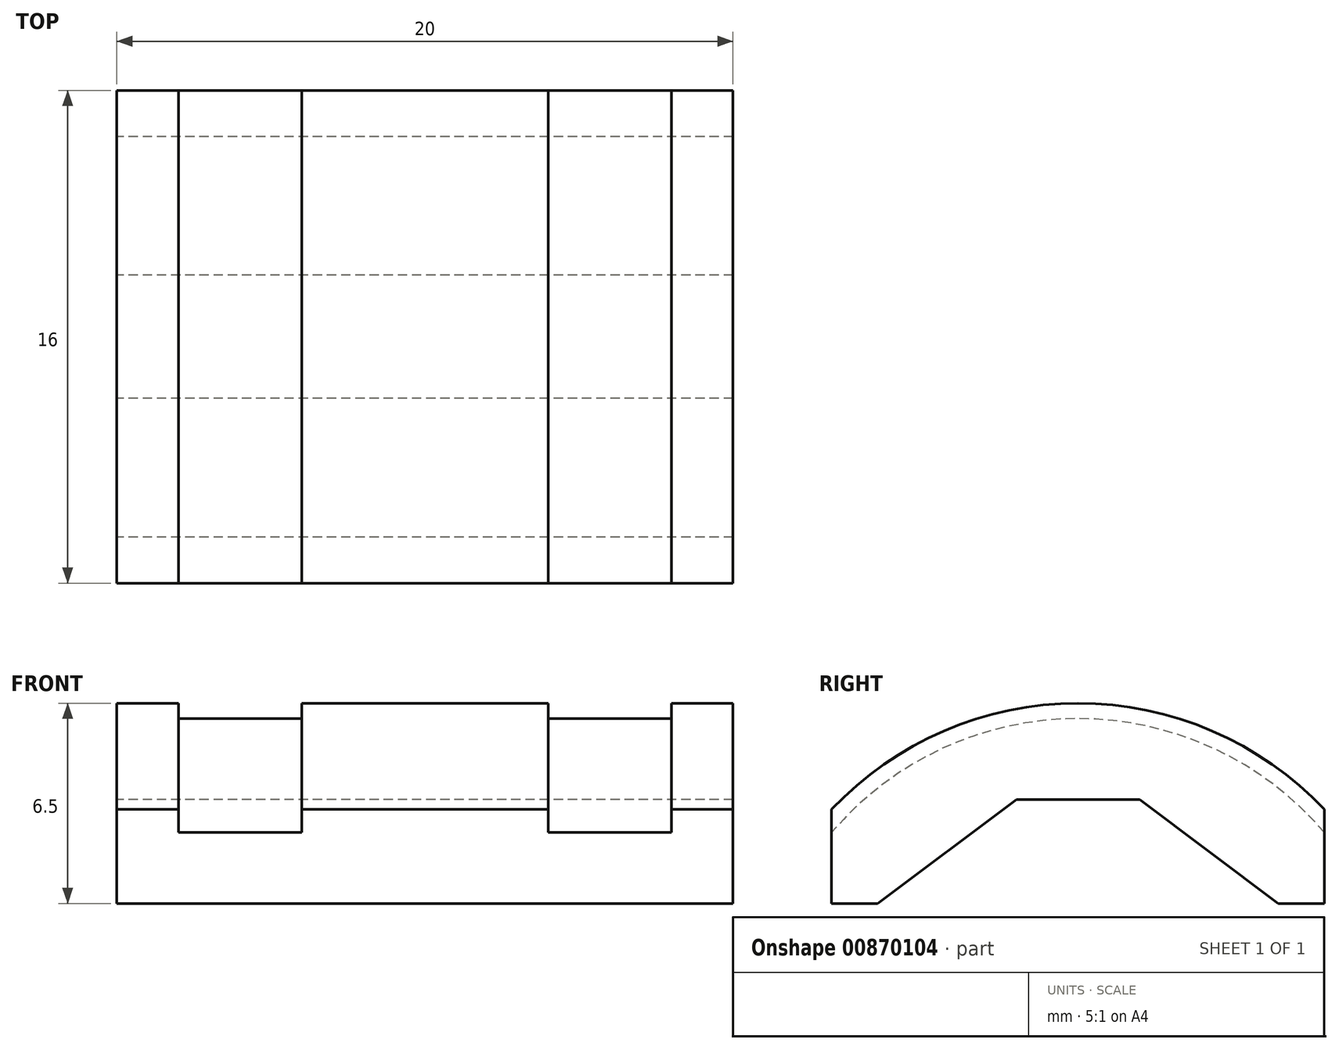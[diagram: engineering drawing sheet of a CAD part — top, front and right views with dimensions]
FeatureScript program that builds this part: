
annotation { "Feature Type Name" : "Feature", "Feature Type Description" : "" }
export const myFeature = defineFeature(function(context is Context, id is Id, definition is map)
    precondition{}
    {
        {
            var Q0;
            Q0=qCreatedBy(makeId("Front.planeOp"),FACE);
            var sketch = newSketch(context, id + "F0", { "sketchPlane" : qUnion([Q0])});
            skLineSegment(sketch, "E0", {"start": v(0, 7.5) * mm, "end": v(0, 11) * mm});
            skLineSegment(sketch, "E1", {"start": v(0, 11) * mm, "end": v(2, 11) * mm});
            skLineSegment(sketch, "E2", {"start": v(2, 11) * mm, "end": v(2, 10.5) * mm});
            skLineSegment(sketch, "E3", {"start": v(6, 10.5) * mm, "end": v(6, 11) * mm});
            skLineSegment(sketch, "E4", {"start": v(6, 11) * mm, "end": v(14, 11) * mm});
            skLineSegment(sketch, "E5", {"start": v(14, 11) * mm, "end": v(14, 10.5) * mm});
            skLineSegment(sketch, "E6", {"start": v(14, 10.5) * mm, "end": v(18, 10.5) * mm});
            skLineSegment(sketch, "E7", {"start": v(18, 10.5) * mm, "end": v(18, 11) * mm});
            skLineSegment(sketch, "E8", {"start": v(18, 11) * mm, "end": v(20, 11) * mm});
            skLineSegment(sketch, "E9", {"start": v(20, 11) * mm, "end": v(20, 7.5) * mm});
            skLineSegment(sketch, "E10", {"start": v(20, 0) * mm, "end": v(0, 0) * mm, "construction": true});
            skLineSegment(sketch, "E11", {"start": v(2, 10.5) * mm, "end": v(6, 10.5) * mm});
            skLineSegment(sketch, "E12", {"start": v(10, 11) * mm, "end": v(10, 0) * mm, "construction": true});
            skLineSegment(sketch, "E13", {"start": v(0, 7.5) * mm, "end": v(20, 7.5) * mm});
            skSolve(sketch);
        }
        {
            var Q0;
            Q0 = qSketchRegion(id + "F0", true);
            var Q1;
            Q1=sQuery(id+"F0.wireOp",EDGE,"E10");
            revolve(context, id + "F1", {"surfaceOperationType" : NewSurfaceOperationType.NEW, "entities" : qUnion([Q0]), "axis" : qUnion([Q1]), "revolveType" : RevolveType.FULL});
        }
        {
            var Q0;
            Q0=makeQuery(id+"F1.opRevolve","SWEPT_FACE",FACE,{"disambiguationData":[OSD([sQuery(id+"F0.wireOp",EDGE,"E0")])]});
            var sketch = newSketch(context, id + "F2", { "sketchPlane" : qUnion([Q0])});
            skLineSegment(sketch, "E14.bottom", {"start": v(-11, 4.5) * mm, "end": v(11, 4.5) * mm});
            skLineSegment(sketch, "E14.top", {"start": v(-11, -11) * mm, "end": v(11, -11) * mm});
            skLineSegment(sketch, "E14.left", {"start": v(-11, 4.5) * mm, "end": v(-11, -11) * mm});
            skLineSegment(sketch, "E14.right", {"start": v(11, 4.5) * mm, "end": v(11, -11) * mm});
            skLineSegment(sketch, "E15", {"start": v(-11, 4.5) * mm, "end": v(-11, 7.55) * mm});
            skLineSegment(sketch, "E16", {"start": v(-11, 7.55) * mm, "end": v(-8, 7.55) * mm});
            skLineSegment(sketch, "E17", {"start": v(-8, 7.55) * mm, "end": v(-8, 4.5) * mm});
            skLineSegment(sketch, "E18.MirrorCS", {"start": v(11, 7.55) * mm, "end": v(8, 7.55) * mm});
            skLineSegment(sketch, "E19.MirrorCS", {"start": v(8, 7.55) * mm, "end": v(8, 4.5) * mm});
            skLineSegment(sketch, "E20.MirrorCS", {"start": v(11, 4.5) * mm, "end": v(11, 7.55) * mm});
            skLineSegment(sketch, "E21", {"start": v(2, 7.87) * mm, "end": v(6.5, 4.5) * mm});
            skLineSegment(sketch, "E22", {"start": v(-2, 7.87) * mm, "end": v(-6.5, 4.5) * mm});
            skLineSegment(sketch, "E23", {"start": v(2, 7.87) * mm, "end": v(-2, 7.87) * mm});
            skPoint(sketch, "E24.orphan", {"position": v(0, 9.37) * mm});
            skSolve(sketch);
        }
        {
            var Q0;
            Q0 = qSketchRegion(id + "F2", true);
            var Q1;
            Q1=makeQuery(id+"F1.opRevolve","SWEPT_FACE",FACE,{"disambiguationData":[OSD([sQuery(id+"F0.wireOp",EDGE,"E9")])]});
            extrude(context, id + "F3", {"entities" : qUnion([Q0]), "operationType" : NewBodyOperationType.REMOVE, "endBound" : BoundingType.UP_TO_SURFACE, "oppositeDirection" : true, "depth" : 25 * mm, "endBoundEntityFace" : qUnion([Q1]), "offsetDistance" : 25 * mm});
        }
    });
